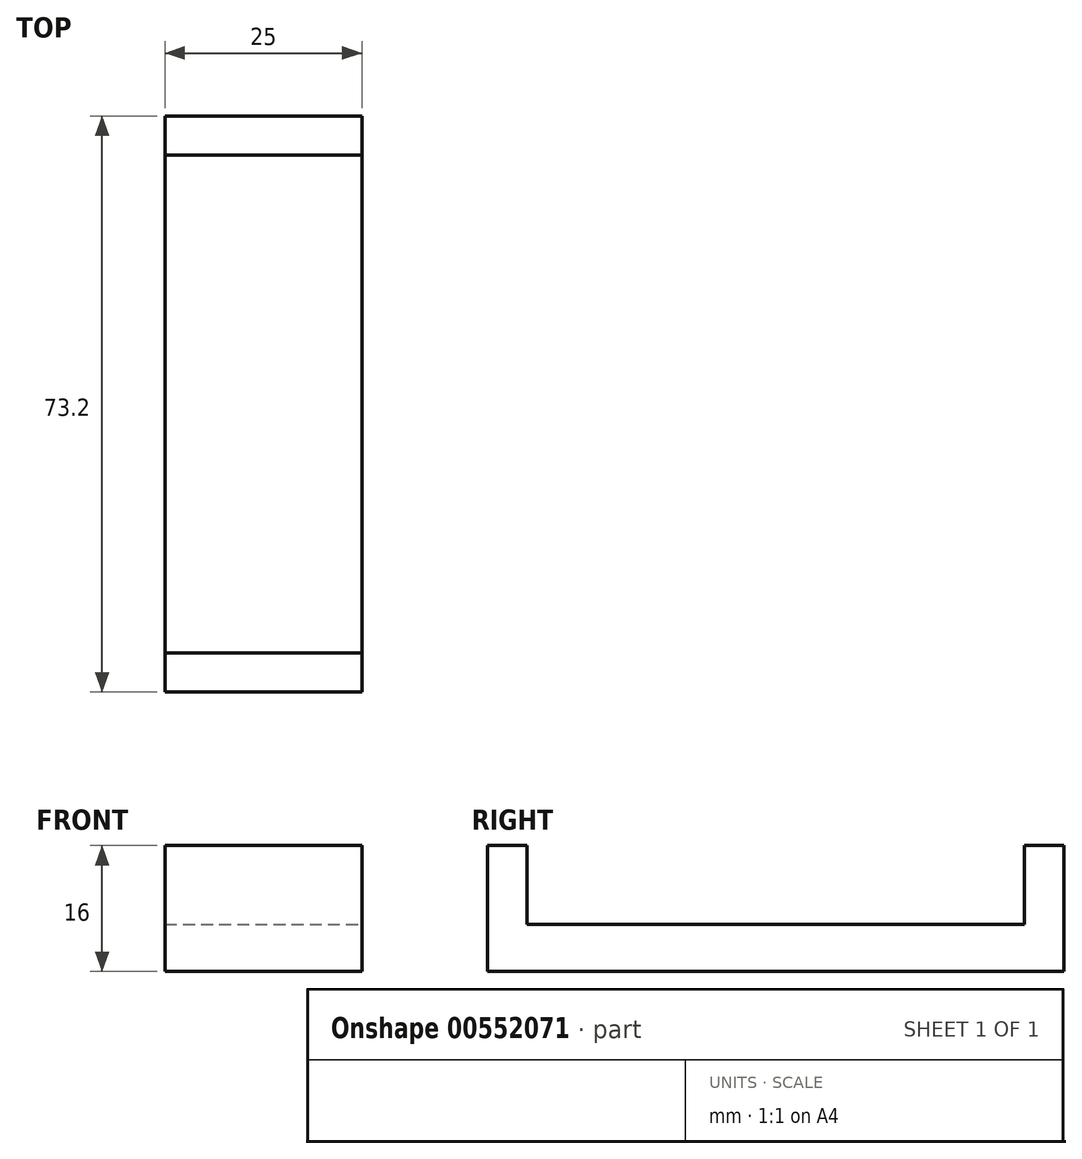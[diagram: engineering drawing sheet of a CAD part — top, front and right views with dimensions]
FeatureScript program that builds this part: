
annotation { "Feature Type Name" : "Feature", "Feature Type Description" : "" }
export const myFeature = defineFeature(function(context is Context, id is Id, definition is map)
    precondition{}
    {
        {
            var Q0;
            Q0=qCreatedBy(makeId("Top.planeOp"),FACE);
            var sketch = newSketch(context, id + "F0", { "sketchPlane" : qUnion([Q0])});
            skLineSegment(sketch, "E0.bottom", {"start": v(12.5, -36.6) * mm, "end": v(-12.5, -36.6) * mm});
            skLineSegment(sketch, "E0.top", {"start": v(12.5, 36.6) * mm, "end": v(-12.5, 36.6) * mm});
            skLineSegment(sketch, "E0.left", {"start": v(12.5, -36.6) * mm, "end": v(12.5, 36.6) * mm});
            skLineSegment(sketch, "E0.right", {"start": v(-12.5, -36.6) * mm, "end": v(-12.5, 36.6) * mm});
            skPoint(sketch, "E0.middle", {"position": v(0, 0) * mm});
            skSolve(sketch);
        }
        {
            var Q0;
            Q0 = qSketchRegion(id + "F0", true);
            extrude(context, id + "F1", {"entities" : qUnion([Q0]), "depth" : 6 * mm, "offsetDistance" : 25 * mm});
        }
        {
            var Q0;
            Q0=makeQuery(id+"F1.opExtrude","CAP_FACE",FACE,{"disambiguationData":[OSD([sQuery(id+"F0.wireOp",EDGE,"E0.bottom"),sQuery(id+"F0.wireOp",EDGE,"E0.top"),sQuery(id+"F0.wireOp",EDGE,"E0.left"),sQuery(id+"F0.wireOp",EDGE,"E0.right")])],"isStart":false});
            var sketch = newSketch(context, id + "F2", { "sketchPlane" : qUnion([Q0])});
            skLineSegment(sketch, "E1.bottom", {"start": v(-12.5, 36.6) * mm, "end": v(12.5, 36.6) * mm});
            skLineSegment(sketch, "E1.top", {"start": v(-12.5, 31.6) * mm, "end": v(12.5, 31.6) * mm});
            skLineSegment(sketch, "E1.left", {"start": v(-12.5, 36.6) * mm, "end": v(-12.5, 31.6) * mm});
            skLineSegment(sketch, "E1.right", {"start": v(12.5, 36.6) * mm, "end": v(12.5, 31.6) * mm});
            skLineSegment(sketch, "E2", {"start": v(0, 0) * mm, "end": v(-36.95, 0) * mm, "construction": true});
            skLineSegment(sketch, "E3.MirrorCS", {"start": v(12.5, -36.6) * mm, "end": v(12.5, -31.6) * mm});
            skLineSegment(sketch, "E4.MirrorCS", {"start": v(-12.5, -36.6) * mm, "end": v(-12.5, -31.6) * mm});
            skLineSegment(sketch, "E5.MirrorCS", {"start": v(-12.5, -36.6) * mm, "end": v(12.5, -36.6) * mm});
            skLineSegment(sketch, "E6.MirrorCS", {"start": v(-12.5, -31.6) * mm, "end": v(12.5, -31.6) * mm});
            skSolve(sketch);
        }
        {
            var Q0;
            Q0 = qSketchRegion(id + "F2", true);
            extrude(context, id + "F3", {"entities" : qUnion([Q0]), "operationType" : NewBodyOperationType.ADD, "depth" : 10 * mm, "offsetDistance" : 25 * mm});
        }
    });
